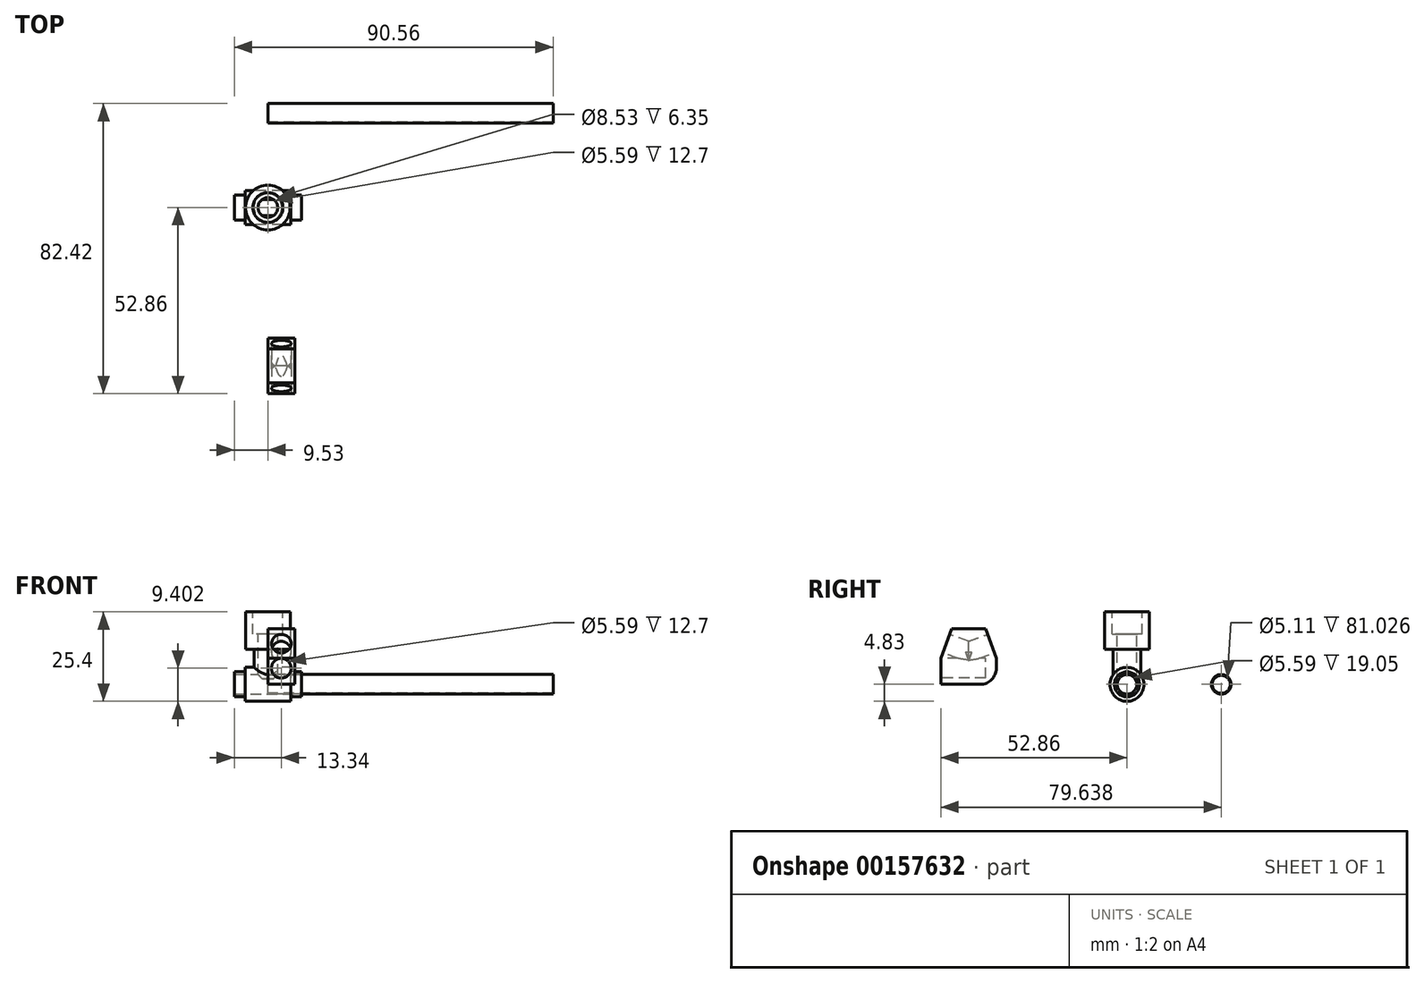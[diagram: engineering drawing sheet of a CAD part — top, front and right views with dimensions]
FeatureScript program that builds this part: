
annotation { "Feature Type Name" : "Feature", "Feature Type Description" : "" }
export const myFeature = defineFeature(function(context is Context, id is Id, definition is map)
    precondition{}
    {
        {
            var Q0;
            Q0=qCreatedBy(makeId("Right.planeOp"),FACE);
            var sketch = newSketch(context, id + "F0", { "sketchPlane" : qUnion([Q0])});
            skCircle(sketch, "E0", {"center": v(0, 0) * mm, "radius": 4.83 * mm});
            skSolve(sketch);
        }
        {
            var Q0;
            Q0=makeQuery(id+"F0.imprint","IMPRINT",FACE,{"disambiguationData":[TD([[makeQuery(id+"F0.imprint","IMPRINT",EDGE,{"derivedFrom":sQuery(id+"F0.wireOp",EDGE,"E0")}),1.0]])]});
            extrude(context, id + "F1", {"entities" : qUnion([Q0]), "depth" : 6.48 * mm, "hasSecondDirection" : true, "secondDirectionOppositeDirection" : true, "secondDirectionDepth" : 6.48 * mm});
        }
        {
            var Q0;
            Q0=makeQuery(id+"F1.opExtrude","CAP_FACE",FACE,{"disambiguationData":[OSD([sQuery(id+"F0.wireOp",EDGE,"E0")])],"isStart":false});
            var sketch = newSketch(context, id + "F2", { "sketchPlane" : qUnion([Q0])});
            skCircle(sketch, "E1", {"center": v(0, 0) * mm, "radius": 3.56 * mm});
            skSolve(sketch);
        }
        {
            var Q0;
            Q0=makeQuery(id+"F2.imprint","IMPRINT",FACE,{"disambiguationData":[TD([[makeQuery(id+"F2.imprint","IMPRINT",EDGE,{"derivedFrom":sQuery(id+"F2.wireOp",EDGE,"E1")}),1.0]])]});
            extrude(context, id + "F3", {"entities" : qUnion([Q0]), "operationType" : NewBodyOperationType.ADD, "depth" : 3.05 * mm});
        }
        {
            var Q0;
            Q0=makeQuery(id+"F1.opExtrude","CAP_FACE",FACE,{"disambiguationData":[OSD([sQuery(id+"F0.wireOp",EDGE,"E0")])],"isStart":true});
            var sketch = newSketch(context, id + "F4", { "sketchPlane" : qUnion([Q0])});
            skCircle(sketch, "E2", {"center": v(0, 0) * mm, "radius": 3.56 * mm});
            skSolve(sketch);
        }
        {
            var Q0;
            Q0=makeQuery(id+"F4.imprint","IMPRINT",FACE,{"disambiguationData":[TD([[makeQuery(id+"F4.imprint","IMPRINT",EDGE,{"derivedFrom":sQuery(id+"F4.wireOp",EDGE,"E2")}),1.0]])]});
            extrude(context, id + "F5", {"entities" : qUnion([Q0]), "operationType" : NewBodyOperationType.ADD, "depth" : 3.05 * mm});
        }
        {
            var Q0;
            Q0=makeQuery(id+"F3.opExtrude","CAP_FACE",FACE,{"disambiguationData":[OSD([sQuery(id+"F2.wireOp",EDGE,"E1")])],"isStart":false});
            var sketch = newSketch(context, id + "F6", { "sketchPlane" : qUnion([Q0])});
            skCircle(sketch, "E3", {"center": v(0, 0) * mm, "radius": 2.8 * mm});
            skSolve(sketch);
        }
        {
            var Q0;
            Q0=makeQuery(id+"F6.imprint","IMPRINT",FACE,{"disambiguationData":[TD([[makeQuery(id+"F6.imprint","IMPRINT",EDGE,{"derivedFrom":sQuery(id+"F6.wireOp",EDGE,"E3")}),1.0]])]});
            extrude(context, id + "F7", {"entities" : qUnion([Q0]), "operationType" : NewBodyOperationType.REMOVE, "oppositeDirection" : true, "depth" : 25.4 * mm});
        }
        {
            var Q0;
            Q0=qCreatedBy(makeId("Top.planeOp"),FACE);
            cPlane(context, id + "F8", {"entities" : qUnion([Q0]), "cplaneType" : CPlaneType.OFFSET, "offset" : 4.83 * mm, "width" : 152.4 * mm, "height" : 152.4 * mm});
        }
        {
            var Q0;
            Q0=qCreatedBy(id+"F8.planeOp",FACE);
            var sketch = newSketch(context, id + "F9", { "sketchPlane" : qUnion([Q0])});
            skCircle(sketch, "E4", {"center": v(0, 0) * mm, "radius": 3.94 * mm});
            skSolve(sketch);
        }
        {
            var Q0;
            Q0=makeQuery(id+"F9.imprint","IMPRINT",FACE,{"disambiguationData":[TD([[makeQuery(id+"F9.imprint","IMPRINT",EDGE,{"derivedFrom":sQuery(id+"F9.wireOp",EDGE,"E4")}),1.0]])]});
            extrude(context, id + "F10", {"entities" : qUnion([Q0]), "operationType" : NewBodyOperationType.ADD, "depth" : 5.08 * mm, "hasSecondDirection" : true, "secondDirectionOppositeDirection" : true, "secondDirectionDepth" : 2.03 * mm});
        }
        {
            var Q0;
            Q0=makeQuery(id+"F10.opExtrude","CAP_FACE",FACE,{"disambiguationData":[OSD([sQuery(id+"F9.wireOp",EDGE,"E4")])],"isStart":false});
            var sketch = newSketch(context, id + "F11", { "sketchPlane" : qUnion([Q0])});
            skCircle(sketch, "E5", {"center": v(0, 0) * mm, "radius": 6.35 * mm});
            skSolve(sketch);
        }
        {
            var Q0;
            Q0=makeQuery(id+"F11.imprint","IMPRINT",FACE,{"disambiguationData":[TD([[makeQuery(id+"F11.imprint","IMPRINT",EDGE,{"derivedFrom":sQuery(id+"F11.wireOp",EDGE,"E5")}),1.0]])]});
            var Q1;
            Q1=makeQuery(id+"F11.imprint","IMPRINT",FACE,{"disambiguationData":[TD([[makeQuery(id+"F11.imprint","IMPRINT",EDGE,{"derivedFrom":makeQuery(id+"F10.opExtrude","CAP_EDGE",EDGE,{"disambiguationData":[OSD([sQuery(id+"F9.wireOp",EDGE,"E4")])],"isStart":false})}),1.0]])]});
            extrude(context, id + "F12", {"entities" : qUnion([Q0, Q1]), "operationType" : NewBodyOperationType.ADD, "depth" : 10.67 * mm});
        }
        {
            var Q0;
            Q0=makeQuery(id+"F12.opExtrude","CAP_FACE",FACE,{"disambiguationData":[OSD([sQuery(id+"F11.wireOp",EDGE,"E5")])],"isStart":false});
            var sketch = newSketch(context, id + "F13", { "sketchPlane" : qUnion([Q0])});
            skCircle(sketch, "E6", {"center": v(0, 0) * mm, "radius": 4.26 * mm});
            skSolve(sketch);
        }
        {
            var Q0;
            Q0=makeQuery(id+"F13.imprint","IMPRINT",FACE,{"disambiguationData":[TD([[makeQuery(id+"F13.imprint","IMPRINT",EDGE,{"derivedFrom":sQuery(id+"F13.wireOp",EDGE,"E6")}),1.0]])]});
            extrude(context, id + "F14", {"entities" : qUnion([Q0]), "operationType" : NewBodyOperationType.REMOVE, "oppositeDirection" : true, "depth" : 6.35 * mm});
        }
        {
            var Q0;
            Q0=makeQuery(id+"F14.boolean.opBoolean","COPY",FACE,{"derivedFrom":makeQuery(id+"F14.opExtrude","CAP_FACE",FACE,{"disambiguationData":[OSD([sQuery(id+"F13.wireOp",EDGE,"E6")])],"isStart":false})});
            var sketch = newSketch(context, id + "F15", { "sketchPlane" : qUnion([Q0])});
            skCircle(sketch, "E7", {"center": v(0, 0) * mm, "radius": 2.8 * mm});
            skSolve(sketch);
        }
        {
            var Q0;
            Q0=makeQuery(id+"F15.imprint","IMPRINT",FACE,{"disambiguationData":[TD([[makeQuery(id+"F15.imprint","IMPRINT",EDGE,{"derivedFrom":sQuery(id+"F15.wireOp",EDGE,"E7")}),1.0]])]});
            extrude(context, id + "F16", {"entities" : qUnion([Q0]), "operationType" : NewBodyOperationType.REMOVE, "oppositeDirection" : true, "depth" : 12.7 * mm});
        }
        {
            var Q0;
            Q0=qCreatedBy(makeId("Right.planeOp"),FACE);
            var sketch = newSketch(context, id + "F17", { "sketchPlane" : qUnion([Q0])});
            skCircle(sketch, "E8", {"center": v(26.78, 0) * mm, "radius": 2.78 * mm});
            skCircle(sketch, "E9", {"center": v(26.78, 0) * mm, "radius": 2.55 * mm});
            skSolve(sketch);
        }
        {
            var Q0;
            Q0=makeQuery(id+"F17.imprint","IMPRINT",FACE,{"disambiguationData":[TD([[makeQuery(id+"F17.imprint","IMPRINT",EDGE,{"derivedFrom":sQuery(id+"F17.wireOp",EDGE,"E8")}),1.0]])]});
            extrude(context, id + "F18", {"entities" : qUnion([Q0]), "depth" : 81.03 * mm});
        }
        {
            var Q0;
            Q0=qCreatedBy(makeId("Right.planeOp"),FACE);
            var sketch = newSketch(context, id + "F19", { "sketchPlane" : qUnion([Q0])});
            skLineSegment(sketch, "E10.bottom", {"start": v(-52.86, 0) * mm, "end": v(-41.69, 0) * mm});
            skLineSegment(sketch, "E10.top", {"start": v(-49.82, 15.75) * mm, "end": v(-40.16, 15.75) * mm});
            skLineSegment(sketch, "E10.left", {"start": v(-52.86, 0) * mm, "end": v(-52.86, 7.37) * mm});
            skLineSegment(sketch, "E10.right", {"start": v(-37.12, 4.57) * mm, "end": v(-37.12, 7.37) * mm});
            skPoint(sketch, "E11.visualSharp", {"position": v(-37.12, 0) * mm});
            skArc(sketch, "E11.filletArc", {"start": v(-41.69, 0) * mm, "mid": v(-38.45, 1.34) * mm, "end": v(-37.12, 4.57) * mm});
            skLineSegment(sketch, "E12", {"start": v(-49.82, 15.75) * mm, "end": v(-52.86, 7.37) * mm});
            skLineSegment(sketch, "E13", {"start": v(-40.16, 15.75) * mm, "end": v(-37.12, 7.37) * mm});
            skLineSegment(sketch, "E14", {"start": v(-44.99, 15.75) * mm, "end": v(-44.99, 0) * mm, "construction": true});
            skLineSegment(sketch, "E15", {"start": v(-44.99, 15.75) * mm, "end": v(-44.99, 9.4) * mm, "construction": true});
            skLineSegment(sketch, "E16", {"start": v(-44.99, 9.4) * mm, "end": v(-51.34, 11.7) * mm, "construction": true});
            skPoint(sketch, "E16.endSnap0", {"position": v(-51.34, 11.56) * mm});
            skLineSegment(sketch, "E17", {"start": v(-44.99, 9.4) * mm, "end": v(-38.64, 11.7) * mm, "construction": true});
            skPoint(sketch, "E17.endSnap0", {"position": v(-38.64, 11.56) * mm});
            skSolve(sketch);
        }
        {
            var Q0;
            Q0=makeQuery(id+"F19.imprint","IMPRINT",FACE,{"disambiguationData":[TD([[makeQuery(id+"F19.imprint","IMPRINT",EDGE,{"derivedFrom":sQuery(id+"F19.wireOp",EDGE,"E10.bottom")}),1.0]])]});
            extrude(context, id + "F20", {"entities" : qUnion([Q0]), "depth" : 7.62 * mm});
        }
        {
            var Q0;
            Q0=makeQuery(id+"F20.opExtrude","SWEPT_FACE",FACE,{"disambiguationData":[OSD([sQuery(id+"F19.wireOp",EDGE,"E10.left")])]});
            var sketch = newSketch(context, id + "F21", { "sketchPlane" : qUnion([Q0])});
            skCircle(sketch, "E18", {"center": v(3.8, 4.57) * mm, "radius": 2.8 * mm});
            skPoint(sketch, "E18.centerSnap0", {"position": v(3.81, 0) * mm});
            skSolve(sketch);
        }
        {
            var Q0;
            Q0=makeQuery(id+"F20.opExtrude","SWEPT_FACE",FACE,{"disambiguationData":[OSD([sQuery(id+"F19.wireOp",EDGE,"E12")])]});
            var sketch = newSketch(context, id + "F22", { "sketchPlane" : qUnion([Q0])});
            skCircle(sketch, "E19", {"center": v(3.81, -6.7) * mm, "radius": 2.8 * mm});
            skPoint(sketch, "E19.centerSnap0", {"position": v(3.81, -11.15) * mm});
            skPoint(sketch, "E19.centerSnap1", {"position": v(0, -6.7) * mm});
            skSolve(sketch);
        }
        {
            var Q0;
            Q0=makeQuery(id+"F20.opExtrude","SWEPT_FACE",FACE,{"disambiguationData":[OSD([sQuery(id+"F19.wireOp",EDGE,"E13")])]});
            var sketch = newSketch(context, id + "F23", { "sketchPlane" : qUnion([Q0])});
            skCircle(sketch, "E20", {"center": v(-3.81, 24.08) * mm, "radius": 2.8 * mm});
            skPoint(sketch, "E20.centerSnap0", {"position": v(0, 24.08) * mm});
            skPoint(sketch, "E20.centerSnap1", {"position": v(-3.81, 19.62) * mm});
            skSolve(sketch);
        }
        {
            var Q0;
            Q0=makeQuery(id+"F21.imprint","IMPRINT",FACE,{"disambiguationData":[TD([[makeQuery(id+"F21.imprint","IMPRINT",EDGE,{"derivedFrom":sQuery(id+"F21.wireOp",EDGE,"E18")}),1.0]])]});
            extrude(context, id + "F24", {"entities" : qUnion([Q0]), "operationType" : NewBodyOperationType.REMOVE, "oppositeDirection" : true, "depth" : 12.7 * mm});
        }
        {
            var Q0;
            Q0=makeQuery(id+"F22.imprint","IMPRINT",FACE,{"disambiguationData":[TD([[makeQuery(id+"F22.imprint","IMPRINT",EDGE,{"derivedFrom":sQuery(id+"F22.wireOp",EDGE,"E19")}),1.0]])]});
            extrude(context, id + "F25", {"entities" : qUnion([Q0]), "operationType" : NewBodyOperationType.REMOVE, "oppositeDirection" : true, "depth" : 7.62 * mm});
        }
        {
            var Q0;
            Q0=makeQuery(id+"F23.imprint","IMPRINT",FACE,{"disambiguationData":[TD([[makeQuery(id+"F23.imprint","IMPRINT",EDGE,{"derivedFrom":sQuery(id+"F23.wireOp",EDGE,"E20")}),1.0]])]});
            extrude(context, id + "F26", {"entities" : qUnion([Q0]), "operationType" : NewBodyOperationType.REMOVE, "oppositeDirection" : true, "depth" : 7.62 * mm});
        }
    });
